# Revit family: Plymold-Essentials-Table_Top-Round+
name_source: partatom
category: Furniture
units: mm (PartAtom-declared; Revit-internal decimal feet)

## family parameters
Always vertical = Yes
Cut with Voids When Loaded = No
OmniClass Number = 23.40.20.00
OmniClass Title = General Furniture and Specialties
Render Appearance Source = Family Geometry
Room Calculation Point = No
Shared = No
Work Plane-Based = No

## types (20) — shared parameters
Assembly Code = E2020200
Default Elevation = 0"
Keynote = 12500
Manufacturer = Plymold
Product Documentation Link = https://plymold.com
Revit Model Built By = https://www.servex-us.com
Sustainability = https://plymold.com
TOP EDGE MATERIAL = PLY - Plastic Black
TOP MATERIAL = PLY - Wood Mahogany
Type Comments = Table Tops & Bases
URL = https://plymold.com
zero-valued in all types: Cost

## per-type parameters (varying)
| type | Brand | DE | Description | Diameter | PVC | TPD | WEB2 |
| 60000WEB2 | Solid Beech Table Top | No | Solid Beech Wood Table Top Round - 60”Dia | 60" | No | No | Yes |
| 48000WEB2 | Solid Beech Table Top | No | Solid Beech Wood Table Top Round - 48”Dia | 48" | No | No | Yes |
| 42000WEB2 | Solid Beech Table Top | No | Solid Beech Wood Table Top Round - 42”Dia | 42" | No | No | Yes |
| 36000WEB2 | Solid Beech Table Top | No | Solid Beech Wood Table Top Round - 36”Dia | 36" | No | No | Yes |
| 30000WEB2 | Solid Beech Table Top | No | Solid Beech Wood Table Top Round - 30”Dia | 30" | No | No | Yes |
| 60000PVC | PVC Edge Table Top | No | PVC Table Top Round - 60”Dia | 60" | Yes | No | No |
| 48000PVC | PVC Edge Table Top | No | PVC Table Top Round - 48”Dia | 48" | Yes | No | No |
| 42000PVC | PVC Edge Table Top | No | PVC Table Top Round - 42”Dia | 42" | Yes | No | No |
| 36000PVC | PVC Edge Table Top | No | PVC Table Top Round - 36”Dia | 36" | Yes | No | No |
| 30000PVC | PVC Edge Table Top | No | PVC Table Top Round - 30”Dia | 30" | Yes | No | No |
| 60000TPD | Dur-A-Edge® Table Top | No | Thin Profile Dur-a-Edge Table Top Round - 60”Dia | 60" | No | Yes | No |
| 48000TPD | Dur-A-Edge® Table Top | No | Thin Profile Dur-a-Edge Table Top Round - 48”Dia | 48" | No | Yes | No |
| 42000TPD | Dur-A-Edge® Table Top | No | Thin Profile Dur-a-Edge Table Top Round - 42”Dia | 42" | No | Yes | No |
| 36000TPD | Dur-A-Edge® Table Top | No | Thin Profile Dur-a-Edge Table Top Round - 36”Dia | 36" | No | Yes | No |
| 30000TPD | Dur-A-Edge® Table Top | No | Thin Profile Dur-a-Edge Table Top Round - 30”Dia | 30" | No | Yes | No |
| 60000DE | Dur-A-Edge® Table Top | Yes | Dur-a-Edge Table Top Round Bullnose - 60”Dia | 60" | No | No | No |
| 48000DE | Dur-A-Edge® Table Top | Yes | Dur-a-Edge Table Top Round Bullnose - 48”Dia | 48" | No | No | No |
| 42000DE | Dur-A-Edge® Table Top | Yes | Dur-a-Edge Table Top Round Bullnose - 42”Dia | 42" | No | No | No |
| 36000DE | Dur-A-Edge® Table Top | Yes | Dur-a-Edge Table Top Round Bullnose - 36”Dia | 36" | No | No | No |
| 30000DE | Dur-A-Edge® Table Top | Yes | Dur-a-Edge Table Top Round Bullnose - 30”Dia | 30" | No | No | No |

note: column(s) folded — value = type name in every type: Model

## geometry (parser evidence)
native form markers: Sweep x4
no freeform markers — native parametric forms only
